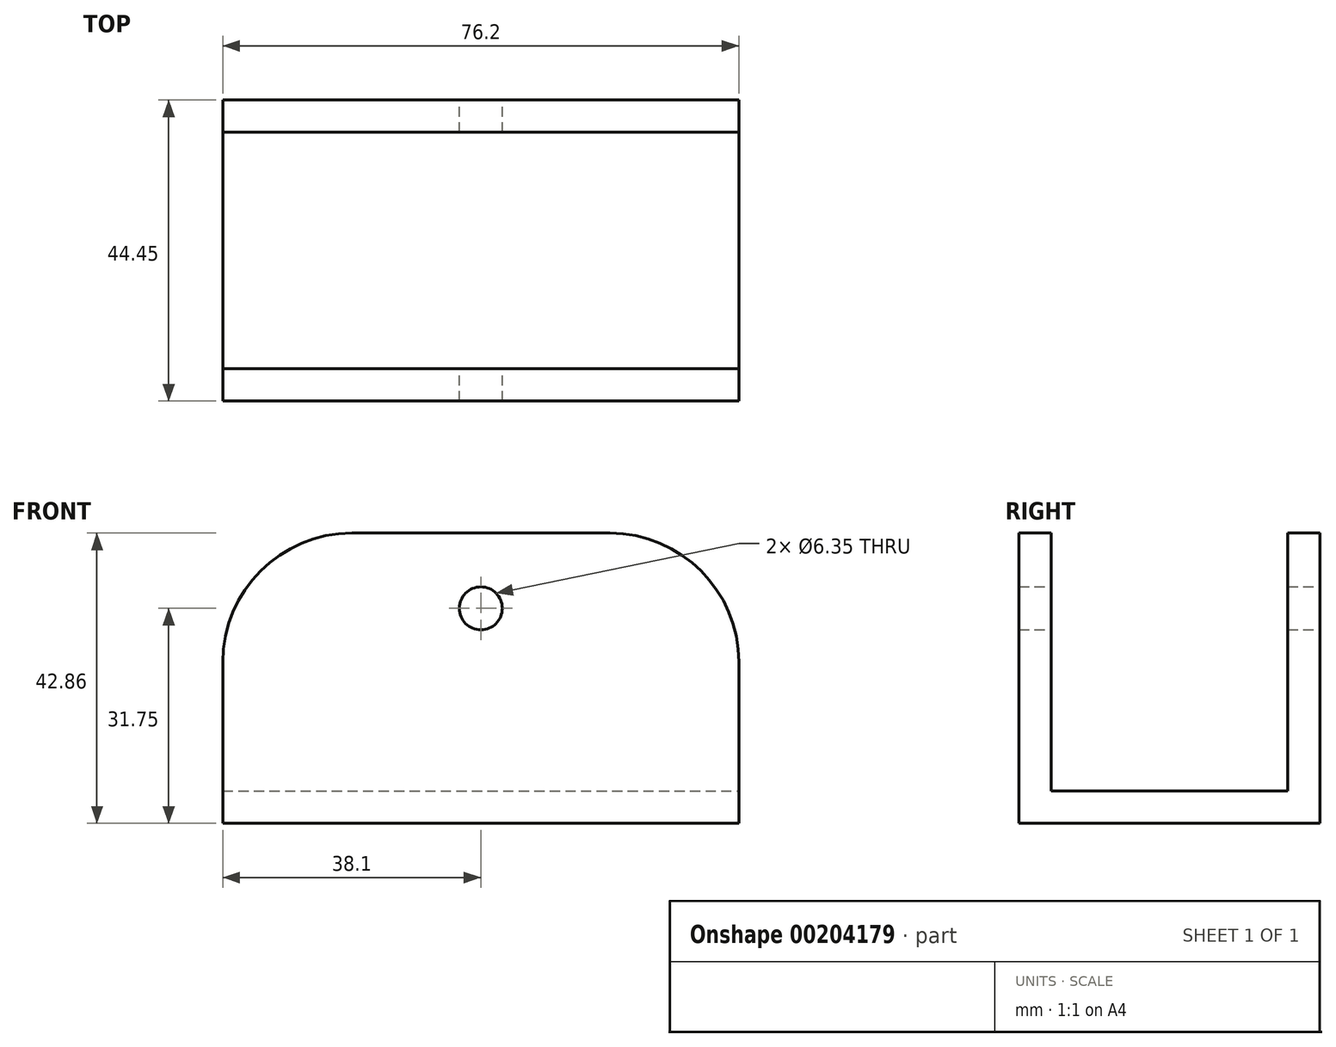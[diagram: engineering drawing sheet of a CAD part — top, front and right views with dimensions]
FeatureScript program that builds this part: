
annotation { "Feature Type Name" : "Feature", "Feature Type Description" : "" }
export const myFeature = defineFeature(function(context is Context, id is Id, definition is map)
    precondition{}
    {
        {
            var Q0;
            Q0=qCreatedBy(makeId("Front.planeOp"),FACE);
            var sketch = newSketch(context, id + "F0", { "sketchPlane" : qUnion([Q0])});
            skLineSegment(sketch, "E0", {"start": v(0, 0) * mm, "end": v(76.2, 0) * mm});
            skLineSegment(sketch, "E1", {"start": v(76.2, 0) * mm, "end": v(76.2, 23.81) * mm});
            skArc(sketch, "E2", {"start": v(76.2, 23.81) * mm, "mid": v(70.62, 37.28) * mm, "end": v(57.15, 42.86) * mm});
            skLineSegment(sketch, "E3", {"start": v(57.15, 42.86) * mm, "end": v(19.05, 42.86) * mm});
            skArc(sketch, "E4", {"start": v(19.05, 42.86) * mm, "mid": v(5.58, 37.28) * mm, "end": v(0, 23.81) * mm});
            skLineSegment(sketch, "E5", {"start": v(0, 23.81) * mm, "end": v(0, 0) * mm});
            skCircle(sketch, "E6", {"center": v(38.1, 31.75) * mm, "radius": 3.18 * mm});
            skSolve(sketch);
        }
        {
            var Q0;
            Q0=makeQuery(id+"F0.imprint","IMPRINT",FACE,{"disambiguationData":[TD([[makeQuery(id+"F0.imprint","IMPRINT",EDGE,{"derivedFrom":sQuery(id+"F0.wireOp",EDGE,"E0")}),1.0]])]});
            extrude(context, id + "F1", {"entities" : qUnion([Q0]), "depth" : 44.45 * mm});
        }
        {
            var Q0;
            Q0=makeQuery(id+"F1.opExtrude","SWEPT_FACE",FACE,{"disambiguationData":[OSD([sQuery(id+"F0.wireOp",EDGE,"E1")])]});
            var sketch = newSketch(context, id + "F2", { "sketchPlane" : qUnion([Q0])});
            skLineSegment(sketch, "E7", {"start": v(-39.69, 4.76) * mm, "end": v(-39.69, 44.98) * mm});
            skLineSegment(sketch, "E8", {"start": v(-39.69, 44.98) * mm, "end": v(-4.76, 44.98) * mm});
            skLineSegment(sketch, "E9", {"start": v(-4.76, 44.98) * mm, "end": v(-4.76, 4.76) * mm});
            skLineSegment(sketch, "E10", {"start": v(-4.76, 4.76) * mm, "end": v(-39.69, 4.76) * mm});
            skSolve(sketch);
        }
        {
            var Q0;
            Q0 = qSketchRegion(id + "F2", true);
            extrude(context, id + "F3", {"entities" : qUnion([Q0]), "operationType" : NewBodyOperationType.REMOVE, "endBound" : BoundingType.THROUGH_ALL, "oppositeDirection" : true, "depth" : 25.4 * mm});
        }
    });
